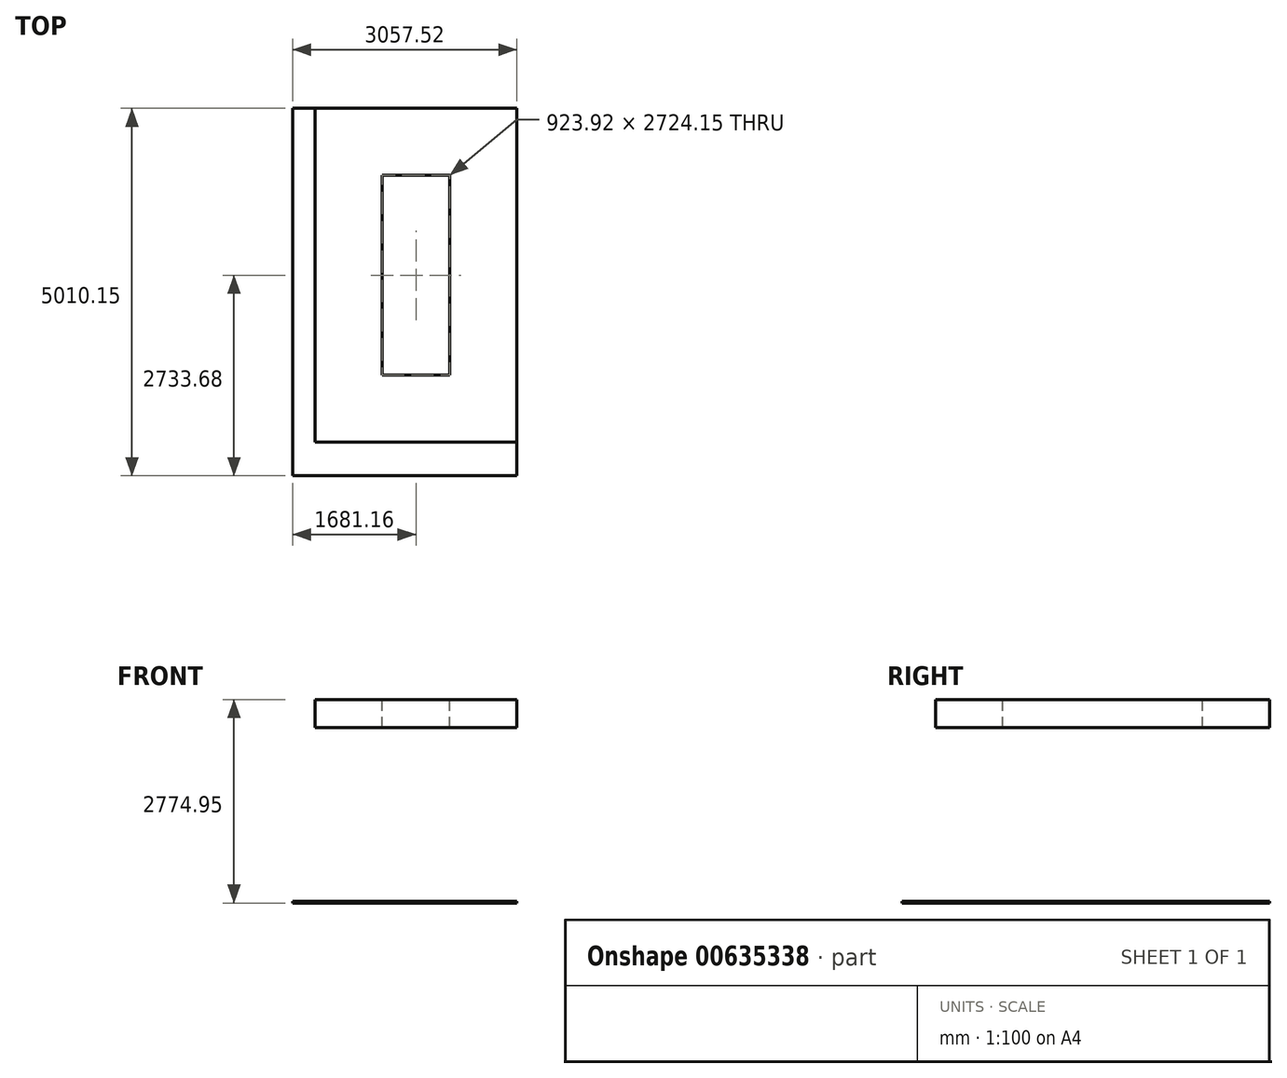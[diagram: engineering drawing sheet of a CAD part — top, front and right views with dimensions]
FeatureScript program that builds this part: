
annotation { "Feature Type Name" : "Feature", "Feature Type Description" : "" }
export const myFeature = defineFeature(function(context is Context, id is Id, definition is map)
    precondition{}
    {
        {
            var Q0;
            Q0=qCreatedBy(makeId("Top.planeOp"),FACE);
            cPlane(context, id + "F0", {"entities" : qUnion([Q0]), "cplaneType" : CPlaneType.OFFSET, "offset" : 2749.55 * mm, "width" : 152.4 * mm, "height" : 152.4 * mm});
        }
        {
            var Q0;
            Q0=qCreatedBy(id+"F0.planeOp",FACE);
            var sketch = newSketch(context, id + "F1", { "sketchPlane" : qUnion([Q0])});
            skLineSegment(sketch, "E0.bottom", {"start": v(-923.93, 2724.15) * mm, "end": v(0, 2724.15) * mm});
            skLineSegment(sketch, "E0.top", {"start": v(-923.93, 0) * mm, "end": v(0, 0) * mm});
            skLineSegment(sketch, "E0.left", {"start": v(-923.93, 2724.15) * mm, "end": v(-923.93, 0) * mm});
            skLineSegment(sketch, "E0.right", {"start": v(0, 2724.15) * mm, "end": v(0, 0) * mm});
            skLineSegment(sketch, "E1.bottom", {"start": v(-1838.33, 3638.55) * mm, "end": v(914.4, 3638.55) * mm});
            skLineSegment(sketch, "E1.top", {"start": v(-1838.33, -914.4) * mm, "end": v(914.4, -914.4) * mm});
            skLineSegment(sketch, "E1.left", {"start": v(-1838.33, 3638.55) * mm, "end": v(-1838.33, -914.4) * mm});
            skLineSegment(sketch, "E1.right", {"start": v(914.4, 3638.55) * mm, "end": v(914.4, -914.4) * mm});
            skSolve(sketch);
        }
        {
            var Q0;
            Q0=makeQuery(id+"F1.imprint","IMPRINT",FACE,{"disambiguationData":[TD([[makeQuery(id+"F1.imprint","IMPRINT",EDGE,{"derivedFrom":sQuery(id+"F1.wireOp",EDGE,"E0.bottom")}),1.0]])]});
            extrude(context, id + "F2", {"entities" : qUnion([Q0]), "oppositeDirection" : true, "depth" : 384.17 * mm, "offsetDistance" : 25.4 * mm});
        }
        {
            var Q0;
            Q0=qCreatedBy(makeId("Top.planeOp"),FACE);
            var sketch = newSketch(context, id + "F3", { "sketchPlane" : qUnion([Q0])});
            skLineSegment(sketch, "E2.bottom", {"start": v(-2143.13, -1371.6) * mm, "end": v(914.4, -1371.6) * mm});
            skLineSegment(sketch, "E2.top", {"start": v(-2143.13, 3638.55) * mm, "end": v(914.4, 3638.55) * mm});
            skLineSegment(sketch, "E2.left", {"start": v(-2143.13, -1371.6) * mm, "end": v(-2143.13, 3638.55) * mm});
            skLineSegment(sketch, "E2.right", {"start": v(914.4, -1371.6) * mm, "end": v(914.4, 3638.55) * mm});
            skSolve(sketch);
        }
        {
            var Q0;
            Q0 = qSketchRegion(id + "F3", true);
            extrude(context, id + "F4", {"entities" : qUnion([Q0]), "oppositeDirection" : true, "depth" : 25.4 * mm, "offsetDistance" : 25.4 * mm});
        }
    });
